# Revit family: RN 92021 Optipress-Aquaplus-Raccordo
name_source: partatom
category: Rohrformteile
units: mm (PartAtom-declared; Revit-internal decimal feet)

## family parameters
Arbeitsebenenbasiert = Nein
Beim Laden mit Abzugskörper schneiden = Nein
Bemaßung runder Anschluss = Durchmesser verwenden
Gemeinsam genutzt = Nein
Immer vertikal = Ja
Teiletyp = Verbindung

## types (13) — shared parameters
1.010.00.2 Blattnummer der Richtlinie = 29
1.010.00.3 Ausgabedatum (Monat) der Richtlinie = 201308
1.010.00.4 Herstellername = R. Nussbaum AG
1.010.00.5 Revisionsdatum der Datei = 20190521
1.010.00.6 Webadresse des Herstellers = http://www.nussbaum.ch
1.100.00.4 Produktbezeichnung = Versorgung
1.110.00.2 Index = 4
1.110.00.4 Produktbezeichnung = Optipress
1.960/3L.00.8 Link (URL) = https://www.nussbaum.ch
29.700.00.4 Produktname = Optipress-A-Anschlussverschraubung, mit Pressmuffe
29.700.00.5 Produktkennung = 2
29.700.00.6 Querschnittsform = 1
29.700.00.7 Nennweitensystem = DN
29.700.00.8 Nenndrucksystem = PN
29.710.02.4 Nenndruck = 16
29.710.02.5 max. zul. Überdruck [hPa] = 1600
29.710.02.7 max. zul. Dauer-Betriebsdruck [hPa] = 1600
29.710.02.9 max. zul. Dauer-Betriebstemperatur [°C] = 95
Connector Visibility = Nein
EnclosingSpace Visibility = Nein

## per-type parameters (varying)
- DN=40: 1.800.00.3 TGA-Nummer=01900400000000000000000000000000000000000000000030000000000000000038; 1.800.00.4 Kommentarfeld=92021.30, Optipress-A-Anschlussverschraubung, mit Pressmuffe, DN=40, L=56; 1.810.00.3 Hersteller-Bestellnummer=92021.3; 1.810.00.4 DATANORM-Nummer=92021.3; 1.810.00.6 GTIN-Nummer=7612945682833; 29.710.02.10 Formstück-Gewicht [kg]=0.358; 29.710.02.3 Benennung=Optipress-A-Anschlussverschraubung, mit Pressmuffe, DN=40, L=56; CONNECTOR0_DIAMETER_dX_0r=40 mm; CONNECTOR0_dX_01=36 mm; CONNECTOR0_ref_dX=36 mm; CONNECTOR1_DIAMETER_dX_0r=50 mm; CONNECTOR1_dX_00=56 mm; CONNECTOR1_dX_01=70 mm; CONNECTOR1_ref_dX=56 mm; Hersteller=R. Nussbaum AG; Modell=92021.3; R. Nussbaum AG 92021.20 de Visibility=Nein; R. Nussbaum AG 92021.22 de Visibility=Nein; R. Nussbaum AG 92021.23 de Visibility=Nein; R. Nussbaum AG 92021.24 de Visibility=Nein; R. Nussbaum AG 92021.25 de Visibility=Nein; R. Nussbaum AG 92021.26 de Visibility=Nein; R. Nussbaum AG 92021.27 de Visibility=Nein; R. Nussbaum AG 92021.28 de Visibility=Nein; R. Nussbaum AG 92021.29 de Visibility=Nein; R. Nussbaum AG 92021.30 de Visibility=Ja; R. Nussbaum AG 92021.33 de Visibility=Nein; R. Nussbaum AG 92021.34 de Visibility=Nein; R. Nussbaum AG 92021.35 de Visibility=Nein; Typenkommentare=Optipress-Aquaplus-Raccordo  DN=40; URL=https://www.nussbaum.ch
- DN=12x15: 1.800.00.3 TGA-Nummer=01900400000000000000000000000000000000000000000030000000000000000037; 1.800.00.4 Kommentarfeld=92021.20, Optipress-A-Anschlussverschraubung, mit Pressmuffe, DN=12x15, L=37; 1.810.00.3 Hersteller-Bestellnummer=92021.2; 1.810.00.4 DATANORM-Nummer=92021.2; 1.810.00.6 GTIN-Nummer=7612945682826; 29.710.02.10 Formstück-Gewicht [kg]=0.056; 29.710.02.3 Benennung=Optipress-A-Anschlussverschraubung, mit Pressmuffe, DN=12x15, L=37; CONNECTOR0_DIAMETER_dX_0r=15 mm  [stored 0.0492126 ft]; CONNECTOR0_dX_01=22 mm; CONNECTOR0_ref_dX=22 mm; CONNECTOR1_DIAMETER_dX_0r=15 mm  [stored 0.0492126 ft]; CONNECTOR1_dX_00=31 mm  [stored 0.101706 ft]; CONNECTOR1_dX_01=44 mm; CONNECTOR1_ref_dX=31 mm  [stored 0.101706 ft]; Hersteller=R. Nussbaum AG; Modell=92021.2; R. Nussbaum AG 92021.20 de Visibility=Ja; R. Nussbaum AG 92021.22 de Visibility=Nein; R. Nussbaum AG 92021.23 de Visibility=Nein; R. Nussbaum AG 92021.24 de Visibility=Nein; R. Nussbaum AG 92021.25 de Visibility=Nein; R. Nussbaum AG 92021.26 de Visibility=Nein; R. Nussbaum AG 92021.27 de Visibility=Nein; R. Nussbaum AG 92021.28 de Visibility=Nein; R. Nussbaum AG 92021.29 de Visibility=Nein; R. Nussbaum AG 92021.30 de Visibility=Nein; R. Nussbaum AG 92021.33 de Visibility=Nein; R. Nussbaum AG 92021.34 de Visibility=Nein; R. Nussbaum AG 92021.35 de Visibility=Nein; Typenkommentare=Optipress-Aquaplus-Raccordo  DN=12x15; URL=https://www.nussbaum.ch
- DN=4: 1.800.00.3 TGA-Nummer=01900400000000000000000000000000000000000000000030000000000000000033; 1.800.00.4 Kommentarfeld=92021.35, Optipress-A-Anschlussverschraubung, mit Pressmuffe, DN=20, L=44; 1.810.00.3 Hersteller-Bestellnummer=92021.35; 1.810.00.4 DATANORM-Nummer=92021.35; 1.810.00.6 GTIN-Nummer=7612945697615; 29.710.02.10 Formstück-Gewicht [kg]=0.09; 29.710.02.3 Benennung=Optipress-A-Anschlussverschraubung, mit Pressmuffe, DN=20, L=44; CONNECTOR0_DIAMETER_dX_0r=20 mm; CONNECTOR0_dX_01=24 mm  [stored 0.0787402 ft]; CONNECTOR0_ref_dX=24 mm  [stored 0.0787402 ft]; CONNECTOR1_DIAMETER_dX_0r=20 mm; CONNECTOR1_dX_00=43 mm; CONNECTOR1_dX_01=52 mm  [stored 0.170604 ft]; CONNECTOR1_ref_dX=43 mm; Hersteller=R. Nussbaum AG; Modell=92021.35; R. Nussbaum AG 92021.20 de Visibility=Nein; R. Nussbaum AG 92021.22 de Visibility=Nein; R. Nussbaum AG 92021.23 de Visibility=Nein; R. Nussbaum AG 92021.24 de Visibility=Nein; R. Nussbaum AG 92021.25 de Visibility=Nein; R. Nussbaum AG 92021.26 de Visibility=Nein; R. Nussbaum AG 92021.27 de Visibility=Nein; R. Nussbaum AG 92021.28 de Visibility=Nein; R. Nussbaum AG 92021.29 de Visibility=Nein; R. Nussbaum AG 92021.30 de Visibility=Nein; R. Nussbaum AG 92021.33 de Visibility=Nein; R. Nussbaum AG 92021.34 de Visibility=Nein; R. Nussbaum AG 92021.35 de Visibility=Ja; Typenkommentare=Optipress-Aquaplus-Raccordo  DN=20; URL=https://www.nussbaum.ch
- DN=1: 1.800.00.3 TGA-Nummer=01900400000000000000000000000000000000000000000030000000000000000032; 1.800.00.4 Kommentarfeld=92021.34, Optipress-A-Anschlussverschraubung, mit Pressmuffe, DN=15, L=33; 1.810.00.3 Hersteller-Bestellnummer=92021.34; 1.810.00.4 DATANORM-Nummer=92021.34; 1.810.00.6 GTIN-Nummer=7612945697608; 29.710.02.10 Formstück-Gewicht [kg]=0.086; 29.710.02.3 Benennung=Optipress-A-Anschlussverschraubung, mit Pressmuffe, DN=15, L=33; CONNECTOR0_DIAMETER_dX_0r=15 mm  [stored 0.0492126 ft]; CONNECTOR0_dX_01=22 mm; CONNECTOR0_ref_dX=22 mm; CONNECTOR1_DIAMETER_dX_0r=25 mm  [stored 0.082021 ft]; CONNECTOR1_dX_00=33 mm; CONNECTOR1_dX_01=41 mm; CONNECTOR1_ref_dX=33 mm; Hersteller=R. Nussbaum AG; Modell=92021.34; R. Nussbaum AG 92021.20 de Visibility=Nein; R. Nussbaum AG 92021.22 de Visibility=Nein; R. Nussbaum AG 92021.23 de Visibility=Nein; R. Nussbaum AG 92021.24 de Visibility=Nein; R. Nussbaum AG 92021.25 de Visibility=Nein; R. Nussbaum AG 92021.26 de Visibility=Nein; R. Nussbaum AG 92021.27 de Visibility=Nein; R. Nussbaum AG 92021.28 de Visibility=Nein; R. Nussbaum AG 92021.29 de Visibility=Nein; R. Nussbaum AG 92021.30 de Visibility=Nein; R. Nussbaum AG 92021.33 de Visibility=Nein; R. Nussbaum AG 92021.34 de Visibility=Ja; R. Nussbaum AG 92021.35 de Visibility=Nein; Typenkommentare=Optipress-Aquaplus-Raccordo  DN=15; URL=https://www.nussbaum.ch
- DN=12x25: 1.800.00.3 TGA-Nummer=01900400000000000000000000000000000000000000000030000000000000000031; 1.800.00.4 Kommentarfeld=92021.33, Optipress-A-Anschlussverschraubung, mit Pressmuffe, DN=12x25, L=33; 1.810.00.3 Hersteller-Bestellnummer=92021.33; 1.810.00.4 DATANORM-Nummer=92021.33; 1.810.00.6 GTIN-Nummer=7612945697592; 29.710.02.10 Formstück-Gewicht [kg]=0.083; 29.710.02.3 Benennung=Optipress-A-Anschlussverschraubung, mit Pressmuffe, DN=12x25, L=33; CONNECTOR0_DIAMETER_dX_0r=12 mm  [stored 0.0393701 ft]; CONNECTOR0_dX_01=22 mm; CONNECTOR0_ref_dX=22 mm; CONNECTOR1_DIAMETER_dX_0r=25 mm  [stored 0.082021 ft]; CONNECTOR1_dX_00=33 mm; CONNECTOR1_dX_01=41 mm; CONNECTOR1_ref_dX=33 mm; Hersteller=R. Nussbaum AG; Modell=92021.33; R. Nussbaum AG 92021.20 de Visibility=Nein; R. Nussbaum AG 92021.22 de Visibility=Nein; R. Nussbaum AG 92021.23 de Visibility=Nein; R. Nussbaum AG 92021.24 de Visibility=Nein; R. Nussbaum AG 92021.25 de Visibility=Nein; R. Nussbaum AG 92021.26 de Visibility=Nein; R. Nussbaum AG 92021.27 de Visibility=Nein; R. Nussbaum AG 92021.28 de Visibility=Nein; R. Nussbaum AG 92021.29 de Visibility=Nein; R. Nussbaum AG 92021.30 de Visibility=Nein; R. Nussbaum AG 92021.33 de Visibility=Ja; R. Nussbaum AG 92021.34 de Visibility=Nein; R. Nussbaum AG 92021.35 de Visibility=Nein; Typenkommentare=Optipress-Aquaplus-Raccordo  DN=12x25; URL=https://www.nussbaum.ch
- DN=2: 1.800.00.3 TGA-Nummer=01900400000000000000000000000000000000000000000030000000000000000030; 1.800.00.4 Kommentarfeld=92021.29, Optipress-A-Anschlussverschraubung, mit Pressmuffe, DN=50, L=58; 1.810.00.3 Hersteller-Bestellnummer=92021.29; 1.810.00.4 DATANORM-Nummer=92021.29; 1.810.00.6 GTIN-Nummer=7612945037619; 29.710.02.10 Formstück-Gewicht [kg]=0.699; 29.710.02.3 Benennung=Optipress-A-Anschlussverschraubung, mit Pressmuffe, DN=50, L=58; CONNECTOR0_DIAMETER_dX_0r=50 mm; CONNECTOR0_dX_01=40 mm; CONNECTOR0_ref_dX=40 mm; CONNECTOR1_DIAMETER_dX_0r=50 mm; CONNECTOR1_dX_00=56 mm; CONNECTOR1_dX_01=72 mm; CONNECTOR1_ref_dX=56 mm; Hersteller=R. Nussbaum AG; Modell=92021.29; R. Nussbaum AG 92021.20 de Visibility=Nein; R. Nussbaum AG 92021.22 de Visibility=Nein; R. Nussbaum AG 92021.23 de Visibility=Nein; R. Nussbaum AG 92021.24 de Visibility=Nein; R. Nussbaum AG 92021.25 de Visibility=Nein; R. Nussbaum AG 92021.26 de Visibility=Nein; R. Nussbaum AG 92021.27 de Visibility=Nein; R. Nussbaum AG 92021.28 de Visibility=Nein; R. Nussbaum AG 92021.29 de Visibility=Ja; R. Nussbaum AG 92021.30 de Visibility=Nein; R. Nussbaum AG 92021.33 de Visibility=Nein; R. Nussbaum AG 92021.34 de Visibility=Nein; R. Nussbaum AG 92021.35 de Visibility=Nein; Typenkommentare=Optipress-Aquaplus-Raccordo  DN=50; URL=https://www.nussbaum.ch
- DN=50: 1.800.00.3 TGA-Nummer=01900400000000000000000000000000000000000000000030000000000000000029; 1.800.00.4 Kommentarfeld=92021.28, Optipress-A-Anschlussverschraubung, mit Pressmuffe, DN=50, L=53; 1.810.00.3 Hersteller-Bestellnummer=92021.28; 1.810.00.4 DATANORM-Nummer=92021.28; 1.810.00.5 StLB-Nummer=671.418; 1.810.00.6 GTIN-Nummer=7612945037602; 29.710.02.10 Formstück-Gewicht [kg]=0.543; 29.710.02.3 Benennung=Optipress-A-Anschlussverschraubung, mit Pressmuffe, DN=50, L=53; CONNECTOR0_DIAMETER_dX_0r=50 mm; CONNECTOR0_dX_01=40 mm; CONNECTOR0_ref_dX=40 mm; CONNECTOR1_DIAMETER_dX_0r=50 mm; CONNECTOR1_dX_00=52 mm  [stored 0.170604 ft]; CONNECTOR1_dX_01=65 mm; CONNECTOR1_ref_dX=52 mm  [stored 0.170604 ft]; Hersteller=R. Nussbaum AG; Modell=92021.28; R. Nussbaum AG 92021.20 de Visibility=Nein; R. Nussbaum AG 92021.22 de Visibility=Nein; R. Nussbaum AG 92021.23 de Visibility=Nein; R. Nussbaum AG 92021.24 de Visibility=Nein; R. Nussbaum AG 92021.25 de Visibility=Nein; R. Nussbaum AG 92021.26 de Visibility=Nein; R. Nussbaum AG 92021.27 de Visibility=Nein; R. Nussbaum AG 92021.28 de Visibility=Ja; R. Nussbaum AG 92021.29 de Visibility=Nein; R. Nussbaum AG 92021.30 de Visibility=Nein; R. Nussbaum AG 92021.33 de Visibility=Nein; R. Nussbaum AG 92021.34 de Visibility=Nein; R. Nussbaum AG 92021.35 de Visibility=Nein; Typenkommentare=Optipress-Aquaplus-Raccordo  DN=50; URL=https://www.nussbaum.ch
- DN=3: 1.800.00.3 TGA-Nummer=01900400000000000000000000000000000000000000000030000000000000000028; 1.800.00.4 Kommentarfeld=92021.27, Optipress-A-Anschlussverschraubung, mit Pressmuffe, DN=40, L=58; 1.810.00.3 Hersteller-Bestellnummer=92021.27; 1.810.00.4 DATANORM-Nummer=92021.27; 1.810.00.5 StLB-Nummer=671.417; 1.810.00.6 GTIN-Nummer=7612945037596; 29.710.02.10 Formstück-Gewicht [kg]=0.35; 29.710.02.3 Benennung=Optipress-A-Anschlussverschraubung, mit Pressmuffe, DN=40, L=58; CONNECTOR0_DIAMETER_dX_0r=40 mm; CONNECTOR0_dX_01=36 mm; CONNECTOR0_ref_dX=36 mm; CONNECTOR1_DIAMETER_dX_0r=40 mm; CONNECTOR1_dX_00=58 mm; CONNECTOR1_dX_01=68 mm; CONNECTOR1_ref_dX=58 mm; Hersteller=R. Nussbaum AG; Modell=92021.27; R. Nussbaum AG 92021.20 de Visibility=Nein; R. Nussbaum AG 92021.22 de Visibility=Nein; R. Nussbaum AG 92021.23 de Visibility=Nein; R. Nussbaum AG 92021.24 de Visibility=Nein; R. Nussbaum AG 92021.25 de Visibility=Nein; R. Nussbaum AG 92021.26 de Visibility=Nein; R. Nussbaum AG 92021.27 de Visibility=Ja; R. Nussbaum AG 92021.28 de Visibility=Nein; R. Nussbaum AG 92021.29 de Visibility=Nein; R. Nussbaum AG 92021.30 de Visibility=Nein; R. Nussbaum AG 92021.33 de Visibility=Nein; R. Nussbaum AG 92021.34 de Visibility=Nein; R. Nussbaum AG 92021.35 de Visibility=Nein; Typenkommentare=Optipress-Aquaplus-Raccordo  DN=40; URL=https://www.nussbaum.ch
- DN=32: 1.800.00.3 TGA-Nummer=01900400000000000000000000000000000000000000000030000000000000000027; 1.800.00.4 Kommentarfeld=92021.26, Optipress-A-Anschlussverschraubung, mit Pressmuffe, DN=32, L=44; 1.810.00.3 Hersteller-Bestellnummer=92021.26; 1.810.00.4 DATANORM-Nummer=92021.26; 1.810.00.5 StLB-Nummer=671.416; 1.810.00.6 GTIN-Nummer=7612945037589; 29.710.02.10 Formstück-Gewicht [kg]=0.216; 29.710.02.3 Benennung=Optipress-A-Anschlussverschraubung, mit Pressmuffe, DN=32, L=44; CONNECTOR0_DIAMETER_dX_0r=32 mm; CONNECTOR0_dX_01=26 mm; CONNECTOR0_ref_dX=26 mm; CONNECTOR1_DIAMETER_dX_0r=40 mm; CONNECTOR1_dX_00=44 mm; CONNECTOR1_dX_01=54 mm; CONNECTOR1_ref_dX=44 mm; Hersteller=R. Nussbaum AG; Modell=92021.26; R. Nussbaum AG 92021.20 de Visibility=Nein; R. Nussbaum AG 92021.22 de Visibility=Nein; R. Nussbaum AG 92021.23 de Visibility=Nein; R. Nussbaum AG 92021.24 de Visibility=Nein; R. Nussbaum AG 92021.25 de Visibility=Nein; R. Nussbaum AG 92021.26 de Visibility=Ja; R. Nussbaum AG 92021.27 de Visibility=Nein; R. Nussbaum AG 92021.28 de Visibility=Nein; R. Nussbaum AG 92021.29 de Visibility=Nein; R. Nussbaum AG 92021.30 de Visibility=Nein; R. Nussbaum AG 92021.33 de Visibility=Nein; R. Nussbaum AG 92021.34 de Visibility=Nein; R. Nussbaum AG 92021.35 de Visibility=Nein; Typenkommentare=Optipress-Aquaplus-Raccordo  DN=32; URL=https://www.nussbaum.ch
- DN=25: 1.800.00.3 TGA-Nummer=01900400000000000000000000000000000000000000000030000000000000000026; 1.800.00.4 Kommentarfeld=92021.25, Optipress-A-Anschlussverschraubung, mit Pressmuffe, DN=25, L=42; 1.810.00.3 Hersteller-Bestellnummer=92021.25; 1.810.00.4 DATANORM-Nummer=92021.25; 1.810.00.5 StLB-Nummer=671.415; 1.810.00.6 GTIN-Nummer=7612945037572; 29.710.02.10 Formstück-Gewicht [kg]=0.167; 29.710.02.3 Benennung=Optipress-A-Anschlussverschraubung, mit Pressmuffe, DN=25, L=42; CONNECTOR0_DIAMETER_dX_0r=25 mm  [stored 0.082021 ft]; CONNECTOR0_dX_01=24 mm  [stored 0.0787402 ft]; CONNECTOR0_ref_dX=24 mm  [stored 0.0787402 ft]; CONNECTOR1_DIAMETER_dX_0r=32 mm; CONNECTOR1_dX_00=42 mm; CONNECTOR1_dX_01=52 mm  [stored 0.170604 ft]; CONNECTOR1_ref_dX=42 mm; R. Nussbaum AG 92021.20 de Visibility=Nein; R. Nussbaum AG 92021.22 de Visibility=Nein; R. Nussbaum AG 92021.23 de Visibility=Nein; R. Nussbaum AG 92021.24 de Visibility=Nein; R. Nussbaum AG 92021.25 de Visibility=Ja; R. Nussbaum AG 92021.26 de Visibility=Nein; R. Nussbaum AG 92021.27 de Visibility=Nein; R. Nussbaum AG 92021.28 de Visibility=Nein; R. Nussbaum AG 92021.29 de Visibility=Nein; R. Nussbaum AG 92021.30 de Visibility=Nein; R. Nussbaum AG 92021.33 de Visibility=Nein; R. Nussbaum AG 92021.34 de Visibility=Nein; R. Nussbaum AG 92021.35 de Visibility=Nein
- DN=20: 1.800.00.3 TGA-Nummer=01900400000000000000000000000000000000000000000030000000000000000025; 1.800.00.4 Kommentarfeld=92021.24, Optipress-A-Anschlussverschraubung, mit Pressmuffe, DN=20, L=39; 1.810.00.3 Hersteller-Bestellnummer=92021.24; 1.810.00.4 DATANORM-Nummer=92021.24; 1.810.00.5 StLB-Nummer=671.414; 1.810.00.6 GTIN-Nummer=7612945037565; 29.710.02.10 Formstück-Gewicht [kg]=0.109; 29.710.02.3 Benennung=Optipress-A-Anschlussverschraubung, mit Pressmuffe, DN=20, L=39; CONNECTOR0_DIAMETER_dX_0r=20 mm; CONNECTOR0_dX_01=24 mm  [stored 0.0787402 ft]; CONNECTOR0_ref_dX=24 mm  [stored 0.0787402 ft]; CONNECTOR1_DIAMETER_dX_0r=25 mm  [stored 0.082021 ft]; CONNECTOR1_dX_00=39 mm; CONNECTOR1_dX_01=47 mm; CONNECTOR1_ref_dX=39 mm; R. Nussbaum AG 92021.20 de Visibility=Nein; R. Nussbaum AG 92021.22 de Visibility=Nein; R. Nussbaum AG 92021.23 de Visibility=Nein; R. Nussbaum AG 92021.24 de Visibility=Ja; R. Nussbaum AG 92021.25 de Visibility=Nein; R. Nussbaum AG 92021.26 de Visibility=Nein; R. Nussbaum AG 92021.27 de Visibility=Nein; R. Nussbaum AG 92021.28 de Visibility=Nein; R. Nussbaum AG 92021.29 de Visibility=Nein; R. Nussbaum AG 92021.30 de Visibility=Nein; R. Nussbaum AG 92021.33 de Visibility=Nein; R. Nussbaum AG 92021.34 de Visibility=Nein; R. Nussbaum AG 92021.35 de Visibility=Nein
- DN=15: 1.800.00.3 TGA-Nummer=01900400000000000000000000000000000000000000000030000000000000000024; 1.800.00.4 Kommentarfeld=92021.23, Optipress-A-Anschlussverschraubung, mit Pressmuffe, DN=15, L=37; 1.810.00.3 Hersteller-Bestellnummer=92021.23; 1.810.00.4 DATANORM-Nummer=92021.23; 1.810.00.5 StLB-Nummer=671.413; 1.810.00.6 GTIN-Nummer=7612945037558; 29.710.02.10 Formstück-Gewicht [kg]=0.075; 29.710.02.3 Benennung=Optipress-A-Anschlussverschraubung, mit Pressmuffe, DN=15, L=37; CONNECTOR0_DIAMETER_dX_0r=15 mm  [stored 0.0492126 ft]; CONNECTOR0_dX_01=22 mm; CONNECTOR0_ref_dX=22 mm; CONNECTOR1_DIAMETER_dX_0r=20 mm; CONNECTOR1_dX_00=37 mm; CONNECTOR1_dX_01=45 mm  [stored 0.147638 ft]; CONNECTOR1_ref_dX=37 mm; Hersteller=R. Nussbaum AG; Modell=92021.23; R. Nussbaum AG 92021.20 de Visibility=Nein; R. Nussbaum AG 92021.22 de Visibility=Nein; R. Nussbaum AG 92021.23 de Visibility=Ja; R. Nussbaum AG 92021.24 de Visibility=Nein; R. Nussbaum AG 92021.25 de Visibility=Nein; R. Nussbaum AG 92021.26 de Visibility=Nein; R. Nussbaum AG 92021.27 de Visibility=Nein; R. Nussbaum AG 92021.28 de Visibility=Nein; R. Nussbaum AG 92021.29 de Visibility=Nein; R. Nussbaum AG 92021.30 de Visibility=Nein; R. Nussbaum AG 92021.33 de Visibility=Nein; R. Nussbaum AG 92021.34 de Visibility=Nein; R. Nussbaum AG 92021.35 de Visibility=Nein; Typenkommentare=Optipress-Aquaplus-Raccordo  DN=15; URL=https://www.nussbaum.ch
- DN=12x20: 1.800.00.3 TGA-Nummer=01900400000000000000000000000000000000000000000030000000000000000023; 1.800.00.4 Kommentarfeld=92021.22, Optipress-A-Anschlussverschraubung, mit Pressmuffe, DN=12x20, L=34; 1.810.00.3 Hersteller-Bestellnummer=92021.22; 1.810.00.4 DATANORM-Nummer=92021.22; 1.810.00.5 StLB-Nummer=671.412; 1.810.00.6 GTIN-Nummer=7612945037541; 29.710.02.10 Formstück-Gewicht [kg]=0.073; 29.710.02.3 Benennung=Optipress-A-Anschlussverschraubung, mit Pressmuffe, DN=12x20, L=34; CONNECTOR0_DIAMETER_dX_0r=12 mm  [stored 0.0393701 ft]; CONNECTOR0_dX_01=22 mm; CONNECTOR0_ref_dX=22 mm; CONNECTOR1_DIAMETER_dX_0r=20 mm; CONNECTOR1_dX_00=34 mm; CONNECTOR1_dX_01=42 mm; CONNECTOR1_ref_dX=34 mm; Hersteller=R. Nussbaum AG; Modell=92021.22; R. Nussbaum AG 92021.20 de Visibility=Nein; R. Nussbaum AG 92021.22 de Visibility=Ja; R. Nussbaum AG 92021.23 de Visibility=Nein; R. Nussbaum AG 92021.24 de Visibility=Nein; R. Nussbaum AG 92021.25 de Visibility=Nein; R. Nussbaum AG 92021.26 de Visibility=Nein; R. Nussbaum AG 92021.27 de Visibility=Nein; R. Nussbaum AG 92021.28 de Visibility=Nein; R. Nussbaum AG 92021.29 de Visibility=Nein; R. Nussbaum AG 92021.30 de Visibility=Nein; R. Nussbaum AG 92021.33 de Visibility=Nein; R. Nussbaum AG 92021.34 de Visibility=Nein; R. Nussbaum AG 92021.35 de Visibility=Nein; Typenkommentare=Optipress-Aquaplus-Raccordo  DN=12x20; URL=https://www.nussbaum.ch

note: [stored X ft] marks values corroborated as IEEE doubles in the binary element streams (Revit-internal decimal feet)

## geometry (parser evidence)
native form markers: Sweep x2
no freeform markers — native parametric forms only
